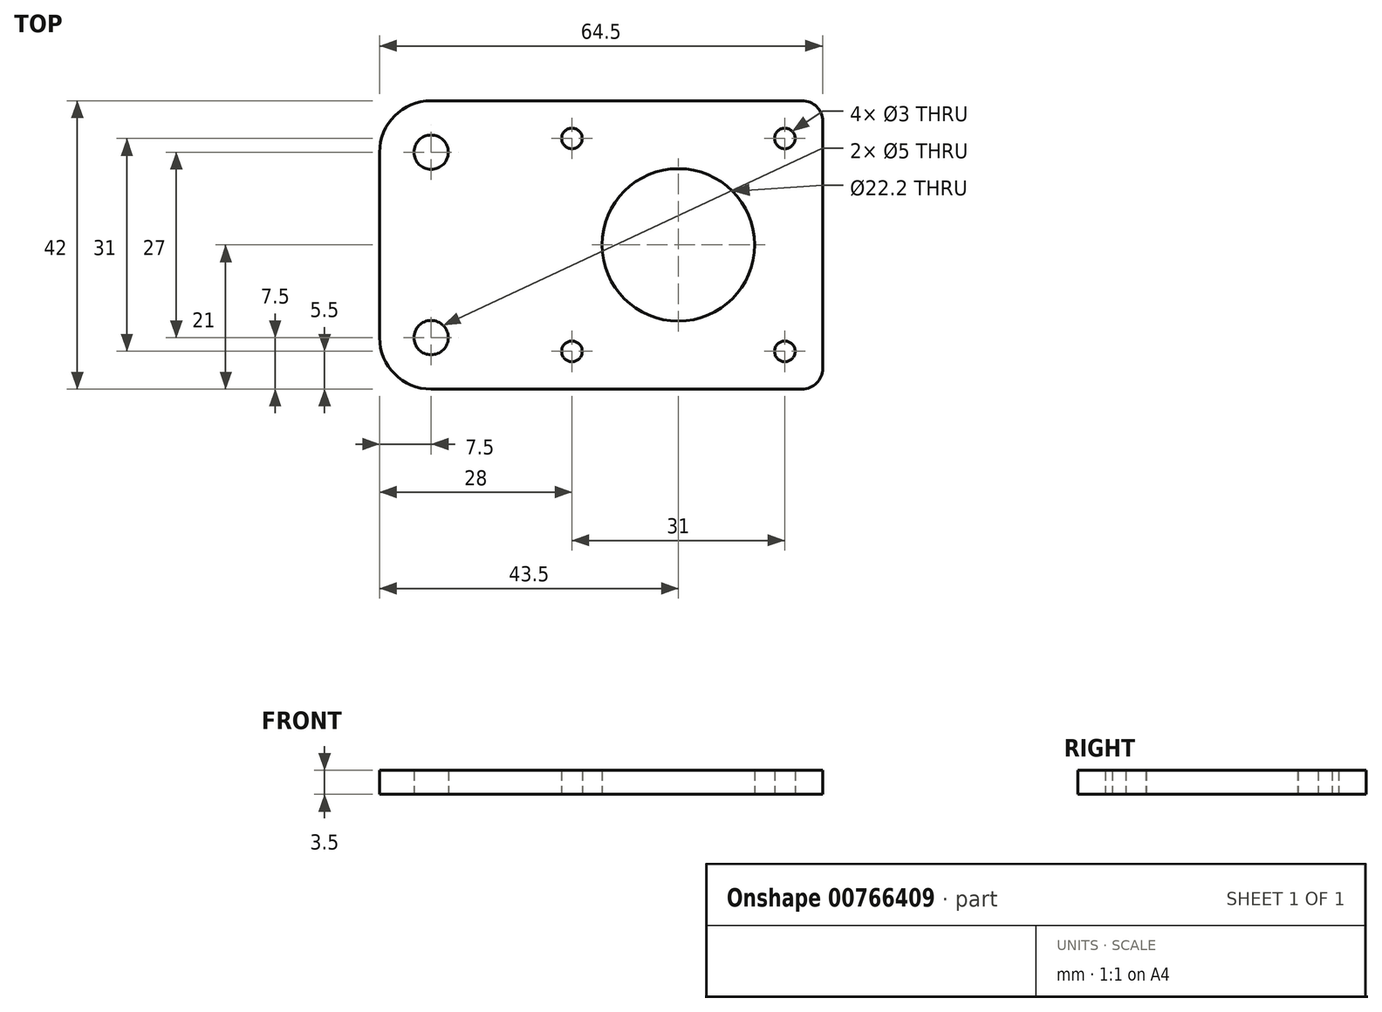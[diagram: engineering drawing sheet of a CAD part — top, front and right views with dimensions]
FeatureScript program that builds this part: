
annotation { "Feature Type Name" : "Feature", "Feature Type Description" : "" }
export const myFeature = defineFeature(function(context is Context, id is Id, definition is map)
    precondition{}
    {
        {
            var Q0;
            Q0=qCreatedBy(makeId("Top.planeOp"),FACE);
            var sketch = newSketch(context, id + "F0", { "sketchPlane" : qUnion([Q0])});
            skLineSegment(sketch, "E0.bottom", {"start": v(-21.1, 21) * mm, "end": v(17.9, 21) * mm});
            skLineSegment(sketch, "E0.top", {"start": v(-21.1, -21) * mm, "end": v(17.9, -21) * mm});
            skLineSegment(sketch, "E0.right", {"start": v(20.9, 18) * mm, "end": v(20.9, -18) * mm});
            skLineSegment(sketch, "E1", {"start": v(-21.1, 21) * mm, "end": v(20.9, -21) * mm, "construction": true});
            skLineSegment(sketch, "E2", {"start": v(-21.1, -21) * mm, "end": v(20.9, 21) * mm, "construction": true});
            skCircle(sketch, "E3", {"center": v(-0.1, 0) * mm, "radius": 11.1 * mm});
            skLineSegment(sketch, "E4", {"start": v(-0.1, 0) * mm, "end": v(-21.1, 0) * mm, "construction": true});
            skLineSegment(sketch, "E5.top", {"start": v(-21.1, -21) * mm, "end": v(-15.6, -21) * mm});
            skLineSegment(sketch, "E5.left", {"start": v(-21.1, 21) * mm, "end": v(-21.1, -21) * mm});
            skLineSegment(sketch, "E5.right", {"start": v(-15.6, 21) * mm, "end": v(-15.6, -21) * mm, "construction": true});
            skLineSegment(sketch, "E6.right", {"start": v(15.4, 21) * mm, "end": v(15.4, -21) * mm, "construction": true});
            skCircle(sketch, "E7", {"center": v(-15.6, 15.5) * mm, "radius": 1.5 * mm});
            skCircle(sketch, "E8", {"center": v(-15.6, -15.5) * mm, "radius": 1.5 * mm});
            skCircle(sketch, "E9", {"center": v(15.4, -15.5) * mm, "radius": 1.5 * mm});
            skCircle(sketch, "E10", {"center": v(15.4, 15.5) * mm, "radius": 1.5 * mm});
            skLineSegment(sketch, "E11.bottom", {"start": v(-21.1, 21) * mm, "end": v(-36.1, 21) * mm});
            skLineSegment(sketch, "E11.top", {"start": v(-21.1, -21) * mm, "end": v(-36.1, -21) * mm});
            skLineSegment(sketch, "E11.right", {"start": v(-36.1, 21) * mm, "end": v(-36.1, -21) * mm, "construction": true});
            skCircle(sketch, "E12", {"center": v(-36.1, 13.5) * mm, "radius": 2.5 * mm});
            skCircle(sketch, "E13", {"center": v(-36.1, -13.5) * mm, "radius": 2.5 * mm});
            skPoint(sketch, "E14.visualSharp", {"position": v(20.9, 21) * mm});
            skArc(sketch, "E14.filletArc", {"start": v(20.9, 18) * mm, "mid": v(20.03, 20.12) * mm, "end": v(17.9, 21) * mm});
            skPoint(sketch, "E15.visualSharp", {"position": v(20.9, -21) * mm});
            skArc(sketch, "E15.filletArc", {"start": v(17.9, -21) * mm, "mid": v(20.03, -20.12) * mm, "end": v(20.9, -18) * mm});
            skLineSegment(sketch, "E16.bottom", {"start": v(-36.1, 21) * mm, "end": v(-36.1, 21) * mm});
            skLineSegment(sketch, "E16.top", {"start": v(-36.1, -21) * mm, "end": v(-36.1, -21) * mm});
            skLineSegment(sketch, "E16.left", {"start": v(-36.1, 21) * mm, "end": v(-36.1, -21) * mm});
            skLineSegment(sketch, "E16.right", {"start": v(-43.6, 13.5) * mm, "end": v(-43.6, -13.5) * mm});
            skPoint(sketch, "E17.visualSharp", {"position": v(-43.6, -21) * mm});
            skArc(sketch, "E17.filletArc", {"start": v(-43.6, -13.5) * mm, "mid": v(-41.4, -18.8) * mm, "end": v(-36.1, -21) * mm});
            skPoint(sketch, "E18.visualSharp", {"position": v(-43.6, 21) * mm});
            skArc(sketch, "E18.filletArc", {"start": v(-36.1, 21) * mm, "mid": v(-41.4, 18.8) * mm, "end": v(-43.6, 13.5) * mm});
            skSolve(sketch);
        }
        {
            var Q0;
            Q0 = qSketchRegion(id + "F0", true);
            extrude(context, id + "F1", {"entities" : qUnion([Q0]), "depth" : 3.5 * mm, "offsetDistance" : 25 * mm});
        }
    });
